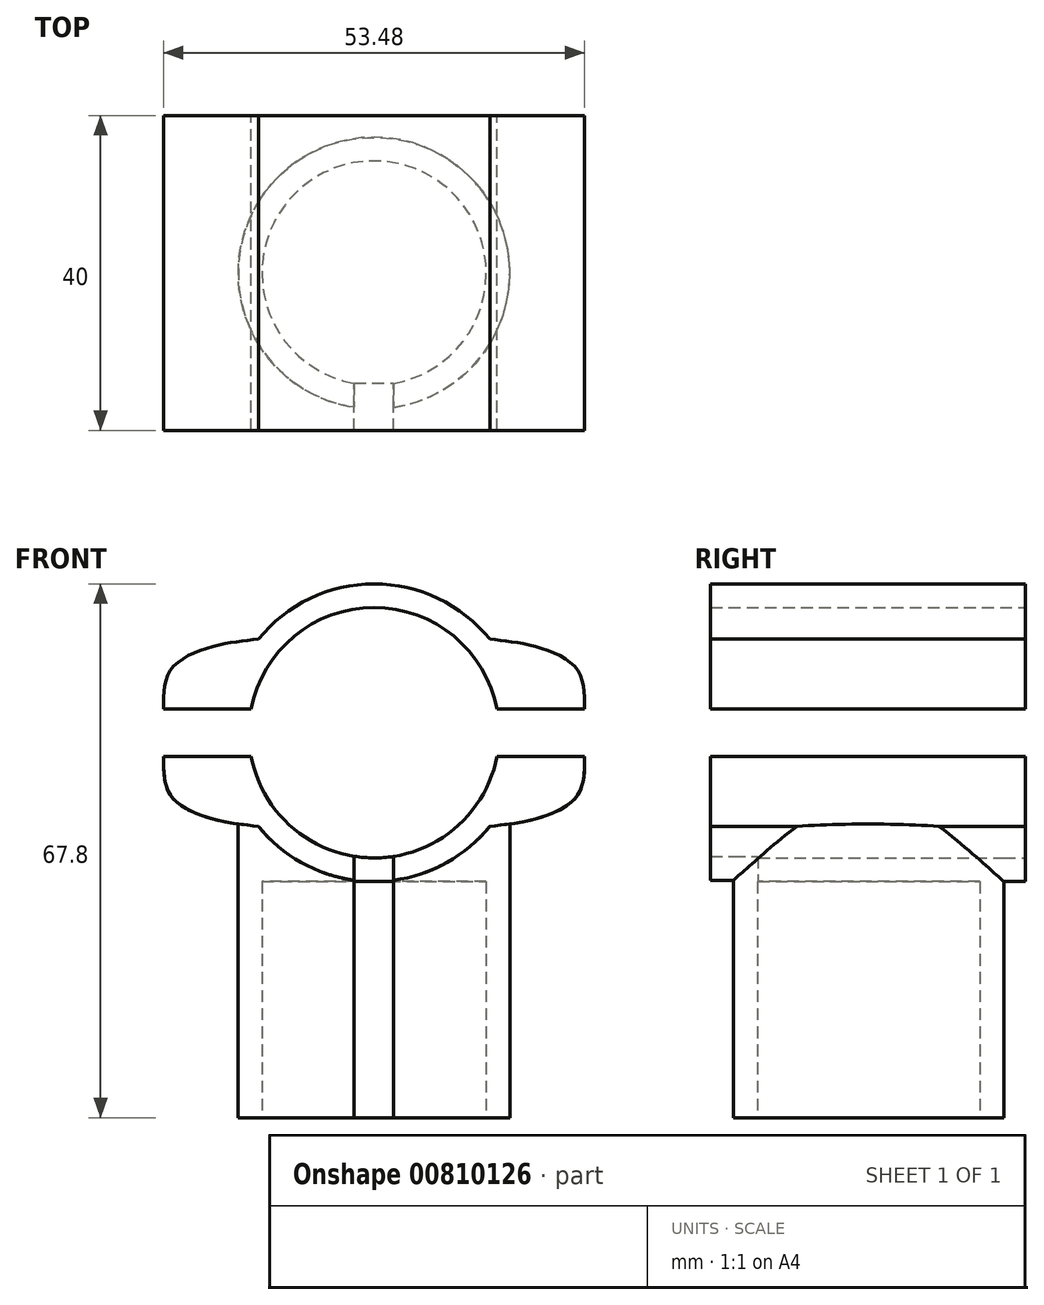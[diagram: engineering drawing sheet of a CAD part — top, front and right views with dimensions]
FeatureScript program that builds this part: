
annotation { "Feature Type Name" : "Feature", "Feature Type Description" : "" }
export const myFeature = defineFeature(function(context is Context, id is Id, definition is map)
    precondition{}
    {
        {
            var Q0;
            Q0=qCreatedBy(makeId("Front.planeOp"),FACE);
            var sketch = newSketch(context, id + "F0", { "sketchPlane" : qUnion([Q0])});
            skLineSegment(sketch, "E0", {"start": v(14.25, 0) * mm, "end": v(14.25, 30) * mm});
            skLineSegment(sketch, "E1", {"start": v(17.25, 0) * mm, "end": v(14.25, 0) * mm});
            skLineSegment(sketch, "E2", {"start": v(0, 0) * mm, "end": v(0, 30) * mm});
            skLineSegment(sketch, "E3", {"start": v(-26.73, 51.9) * mm, "end": v(-15.61, 51.9) * mm});
            skFitSpline(sketch, "E4", {"points": [v(-26.73, 51.9) * mm, v(-25.75, 57) * mm, v(-20.14, 59.94) * mm, v(-14.7, 60.79) * mm], "startDerivative": vector(-0.13, 17.54) * mm, "endDerivative": vector(15.85, 1.61) * mm});
            skFitSpline(sketch, "E5.MirrorCS", {"points": [v(26.73, 51.9) * mm, v(25.75, 57) * mm, v(20.14, 59.94) * mm, v(14.7, 60.79) * mm], "startDerivative": vector(0.13, 17.54) * mm, "endDerivative": vector(-15.85, 1.61) * mm});
            skLineSegment(sketch, "E6.MirrorCS", {"start": v(26.73, 51.9) * mm, "end": v(15.61, 51.9) * mm});
            skArc(sketch, "E7.trimOffspring", {"start": v(15.61, 51.9) * mm, "mid": v(0, 64.8) * mm, "end": v(-15.61, 51.9) * mm});
            skArc(sketch, "E8.trimOffspring", {"start": v(14.7, 60.79) * mm, "mid": v(0, 67.8) * mm, "end": v(-14.7, 60.79) * mm});
            skLineSegment(sketch, "E9", {"start": v(17.25, 0) * mm, "end": v(17.25, 45.7) * mm});
            skLineSegment(sketch, "E10", {"start": v(14.25, 30) * mm, "end": v(0, 30) * mm});
            skLineSegment(sketch, "E11", {"start": v(17.25, 45.7) * mm, "end": v(0, 45.7) * mm});
            skLineSegment(sketch, "E12", {"start": v(0, 45.7) * mm, "end": v(0, 30) * mm});
            skSolve(sketch);
        }
        {
            var Q0;
            Q0=qCreatedBy(makeId("Front.planeOp"),FACE);
            var sketch = newSketch(context, id + "F1", { "sketchPlane" : qUnion([Q0])});
            skCircle(sketch, "E13", {"center": v(0, 48.9) * mm, "radius": 15.9 * mm});
            skSolve(sketch);
        }
        {
            var Q0;
            Q0=makeQuery(id+"F0.imprint","IMPRINT",FACE,{"disambiguationData":[TD([[makeQuery(id+"F0.imprint","IMPRINT",EDGE,{"derivedFrom":sQuery(id+"F0.wireOp",EDGE,"E0")}),-1.0]])]});
            var Q1;
            Q1=sQuery(id+"F0.wireOp",EDGE,"E2");
            revolve(context, id + "F2", {"surfaceOperationType" : NewSurfaceOperationType.NEW, "entities" : qUnion([Q0]), "axis" : qUnion([Q1]), "revolveType" : RevolveType.FULL});
        }
        {
            var Q0;
            Q0=qCreatedBy(makeId("Front.planeOp"),FACE);
            var sketch = newSketch(context, id + "F3", { "sketchPlane" : qUnion([Q0])});
            skLineSegment(sketch, "E14", {"start": v(-14.25, 97.8) * mm, "end": v(-14.25, 67.8) * mm});
            skLineSegment(sketch, "E15", {"start": v(-17.25, 97.8) * mm, "end": v(-14.25, 97.8) * mm});
            skLineSegment(sketch, "E16", {"start": v(0, 97.8) * mm, "end": v(0, 67.8) * mm});
            skLineSegment(sketch, "E17", {"start": v(26.73, 45.9) * mm, "end": v(15.61, 45.9) * mm});
            skFitSpline(sketch, "E18", {"points": [v(26.73, 45.9) * mm, v(25.75, 40.8) * mm, v(20.14, 37.86) * mm, v(14.7, 37.01) * mm], "startDerivative": vector(0.13, -17.54) * mm, "endDerivative": vector(-15.85, -1.61) * mm});
            skFitSpline(sketch, "E19.MirrorCS", {"points": [v(-26.73, 45.9) * mm, v(-25.75, 40.8) * mm, v(-20.14, 37.86) * mm, v(-14.7, 37.01) * mm], "startDerivative": vector(-0.13, -17.54) * mm, "endDerivative": vector(15.85, -1.61) * mm});
            skLineSegment(sketch, "E20.MirrorCS", {"start": v(-26.73, 45.9) * mm, "end": v(-15.61, 45.9) * mm});
            skArc(sketch, "E21.trimOffspring", {"start": v(-15.61, 45.9) * mm, "mid": v(0, 33) * mm, "end": v(15.61, 45.9) * mm});
            skArc(sketch, "E22.trimOffspring", {"start": v(-14.7, 37.01) * mm, "mid": v(0, 30) * mm, "end": v(14.7, 37.01) * mm});
            skSolve(sketch);
        }
        {
            var Q0;
            Q0=makeQuery(id+"F3.imprint","IMPRINT",FACE,{"disambiguationData":[TD([[makeQuery(id+"F3.imprint","IMPRINT",EDGE,{"derivedFrom":sQuery(id+"F3.wireOp",EDGE,"E17")}),1.0]])]});
            var Q1;
            Q1=makeQuery(id+"F0.imprint","IMPRINT",FACE,{"disambiguationData":[TD([[makeQuery(id+"F0.imprint","IMPRINT",EDGE,{"derivedFrom":sQuery(id+"F0.wireOp",EDGE,"E3")}),1.0]])]});
            extrude(context, id + "F4", {"entities" : qUnion([Q0, Q1]), "operationType" : NewBodyOperationType.ADD, "endBound" : BoundingType.SYMMETRIC, "depth" : 40 * mm, "offsetDistance" : 25 * mm});
        }
        {
            var Q0;
            Q0 = qSketchRegion(id + "F1", true);
            extrude(context, id + "F5", {"entities" : qUnion([Q0]), "operationType" : NewBodyOperationType.REMOVE, "endBound" : BoundingType.SYMMETRIC, "depth" : 50 * mm, "offsetDistance" : 25 * mm});
        }
        {
            var Q0;
            Q0=qCreatedBy(makeId("Front.planeOp"),FACE);
            cPlane(context, id + "F6", {"entities" : qUnion([Q0]), "cplaneType" : CPlaneType.OFFSET, "offset" : 40 * mm, "width" : 150 * mm, "height" : 150 * mm});
        }
        {
            var Q0;
            Q0=qCreatedBy(id+"F6.planeOp",FACE);
            var sketch = newSketch(context, id + "F7", { "sketchPlane" : qUnion([Q0])});
            skLineSegment(sketch, "E23", {"start": v(-0.04, -17.45) * mm, "end": v(-0.04, 37.95) * mm});
            skLineSegment(sketch, "E24", {"start": v(-0.04, 37.95) * mm, "end": v(2.46, 37.95) * mm});
            skLineSegment(sketch, "E25", {"start": v(2.46, 37.95) * mm, "end": v(2.46, -17.45) * mm});
            skLineSegment(sketch, "E26", {"start": v(2.46, -17.45) * mm, "end": v(-0.04, -17.45) * mm});
            skLineSegment(sketch, "E27.MirrorCS", {"start": v(-2.54, 37.95) * mm, "end": v(-2.54, -17.45) * mm});
            skLineSegment(sketch, "E28.MirrorCS", {"start": v(-0.04, 37.95) * mm, "end": v(-2.54, 37.95) * mm});
            skLineSegment(sketch, "E29.MirrorCS", {"start": v(-2.54, -17.45) * mm, "end": v(-0.04, -17.45) * mm});
            skSolve(sketch);
        }
        {
            var Q0;
            Q0=makeQuery(id+"F7.imprint","IMPRINT",FACE,{"disambiguationData":[TD([[makeQuery(id+"F7.imprint","IMPRINT",EDGE,{"derivedFrom":sQuery(id+"F7.wireOp",EDGE,"E23")}),-1.0]])]});
            var Q1;
            Q1=makeQuery(id+"F7.imprint","IMPRINT",FACE,{"disambiguationData":[TD([[makeQuery(id+"F7.imprint","IMPRINT",EDGE,{"derivedFrom":sQuery(id+"F7.wireOp",EDGE,"E23")}),1.0]])]});
            extrude(context, id + "F8", {"entities" : qUnion([Q0, Q1]), "operationType" : NewBodyOperationType.REMOVE, "oppositeDirection" : true, "depth" : 26.04 * mm, "offsetDistance" : 25 * mm});
        }
    });
